# Revit family: FF-Victaulic-Exposed-V2703-SSU-LPCB (Hosted)
name_source: partatom
category: Sprinklers
units: mm (PartAtom-declared; Revit-internal decimal feet)

## family parameters
Cut with Voids When Loaded = No
Host = Face
Maintain Annotation Orientation = Yes
Part Type = Normal
Room Calculation Point = Yes
Round Connector Dimension = Use Diameter
Shared = No

## types (6) — shared parameters
Classification.Uniclass.EF.Description = Fire extinguishing supply
Classification.Uniclass.EF.Number = EF_55_30_98
Classification.Uniclass.Pr.Description = Sprinkler heads
Classification.Uniclass.Pr.Number = Pr_70_55_97_84
Classification.Uniclass.Ss.Description = Sprinkler systems
Classification.Uniclass.Ss.Number = Ss_55_30_98_85
Coverage = Standard
Default Elevation = 1219 mm
Description = Exposed Soffit Protection
Diameter = 15  [stored 0.0492126 ft]
FIREFLY - Material = Brass - Forged
K-Factor = 80
Manufacturer = VICTAULIC
Model = V2703
Orifice = Standard
Orifice Size = 15  [stored 0.0492126 ft]
Pressure Class = Standard
Response = Standard
Type Comments = SSU
URL = https://www.victaulic.com

## per-type parameters (varying)
| type | FIREFLY - Finish | Temperature | Temperature Rating |
| 68ºC Brass | Brass | No | 68 °C |
| 68ºC White | White Paint | No | 68 °C |
| 68ºC Black | Flat Black Paint | No | 68 °C |
| 141ºC Brass | Brass | Yes | 141 °C |
| 141ºC Black | Flat Black Paint | Yes | 141 °C |
| 141ºC White | White Paint | Yes | 141 °C |

note: [stored X ft] marks values corroborated as IEEE doubles in the binary element streams (Revit-internal decimal feet)

## geometry (parser evidence)
native form markers: Sweep x12
no freeform markers — native parametric forms only
